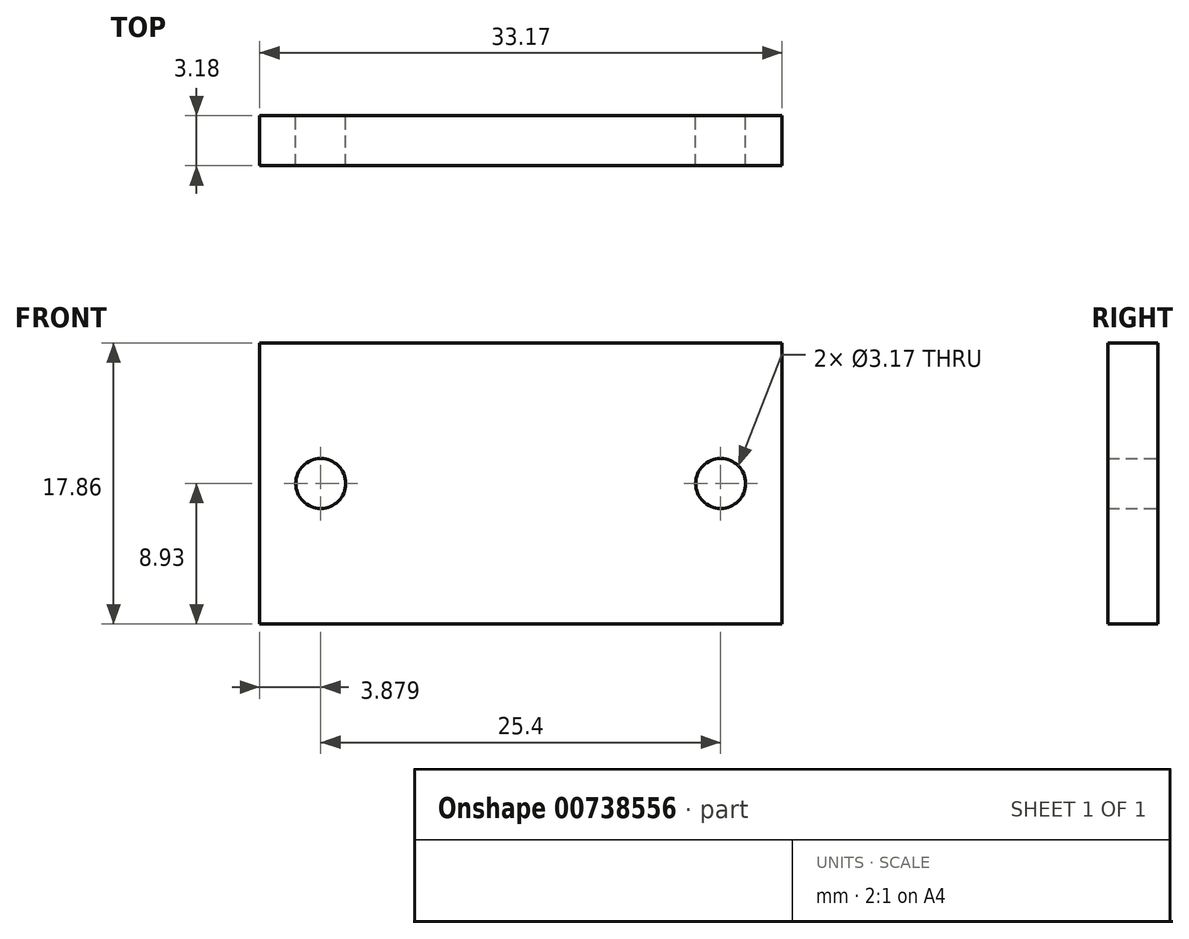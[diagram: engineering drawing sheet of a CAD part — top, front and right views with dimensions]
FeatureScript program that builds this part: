
annotation { "Feature Type Name" : "Feature", "Feature Type Description" : "" }
export const myFeature = defineFeature(function(context is Context, id is Id, definition is map)
    precondition{}
    {
        {
            var Q0;
            Q0=qCreatedBy(makeId("Front.planeOp"),FACE);
            var sketch = newSketch(context, id + "F0", { "sketchPlane" : qUnion([Q0])});
            skLineSegment(sketch, "E0.bottom", {"start": v(-22.43, 22.12) * mm, "end": v(79.17, 22.12) * mm});
            skLineSegment(sketch, "E0.top", {"start": v(-22.43, -22.33) * mm, "end": v(79.17, -22.33) * mm});
            skLineSegment(sketch, "E0.left", {"start": v(-22.43, 22.12) * mm, "end": v(-22.43, -22.33) * mm});
            skLineSegment(sketch, "E0.right", {"start": v(79.17, 22.12) * mm, "end": v(79.17, -22.33) * mm});
            skCircle(sketch, "E1", {"center": v(-9.1, 0) * mm, "radius": 1.59 * mm});
            skCircle(sketch, "E2", {"center": v(16.69, 0) * mm, "radius": 1.59 * mm});
            skCircle(sketch, "E3", {"center": v(42.09, 0) * mm, "radius": 1.59 * mm});
            skCircle(sketch, "E4", {"center": v(59.44, -0.1) * mm, "radius": 1.59 * mm});
            skPoint(sketch, "E4.centerSnap0", {"position": v(79.17, -0.1) * mm});
            skLineSegment(sketch, "E5.bottom", {"start": v(12.81, 8.93) * mm, "end": v(45.98, 8.93) * mm});
            skLineSegment(sketch, "E5.top", {"start": v(12.81, -8.93) * mm, "end": v(45.98, -8.93) * mm});
            skLineSegment(sketch, "E5.left", {"start": v(12.81, 8.93) * mm, "end": v(12.81, -8.93) * mm});
            skLineSegment(sketch, "E5.right", {"start": v(45.98, 8.93) * mm, "end": v(45.98, -8.93) * mm});
            skSolve(sketch);
        }
        {
            var Q0;
            Q0=makeQuery(id+"F0.imprint","IMPRINT",FACE,{"disambiguationData":[TD([[makeQuery(id+"F0.imprint","IMPRINT",EDGE,{"derivedFrom":sQuery(id+"F0.wireOp",EDGE,"E2")}),-1.0]])]});
            extrude(context, id + "F1", {"entities" : qUnion([Q0]), "depth" : 3.17 * mm, "offsetDistance" : 25.4 * mm});
        }
    });
